# Revit family: VTp731 Тройник 90
name_source: partatom
category: Соединительные детали трубопроводов
revit_build: Autodesk Revit 2015 (Build: 20140606_1530(x64)
units: mm (PartAtom-declared; Revit-internal decimal feet)

## types (9) — shared parameters
Группа модели = VTp.700
Изготовитель = VALTEC S.R.L.
Коэффициент K = 0.5
Метод определения потерь = Коэффициент K
Описание = Тройник 90
Таблица коэффициентов K = Angle Valve Threaded

## per-type parameters (varying)
| type | 110 | 20 | 25 | 32 | 40 | 50 | 63 | 75 | 90 | A | B | d | Код по классификатору | Сц |
| 20 | Нет | Да | Нет | Нет | Нет | Нет | Нет | Нет | Нет | 51 мм | 15 мм | 20 мм | VTp.731.0.020 | 26 мм |
| 25 | Нет | Нет | Да | Нет | Нет | Нет | Нет | Нет | Нет | 59 мм | 17 мм | 25 мм | VTp.731.0.025 | 30 мм |
| 40 | Нет | Нет | Нет | Нет | Да | Нет | Нет | Нет | Нет | 89 мм | 21 мм | 40 мм | VTp.731.0.040 | 44 мм |
| 32 | Нет | Нет | Нет | Да | Нет | Нет | Нет | Нет | Нет | 71 мм | 19 мм | 32 мм | VTp.731.0.032 | 36 мм |
| 50 | Нет | Нет | Нет | Нет | Нет | Да | Нет | Нет | Нет | 106 мм | 24 мм | 50 мм | VTp.731.0.050 | 53 мм |
| 63 | Нет | Нет | Нет | Нет | Нет | Нет | Да | Нет | Нет | 128 мм | 26 мм | 63 мм | VTp.731.0.063 | 64 мм |
| 75 | Нет | Нет | Нет | Нет | Нет | Нет | Нет | Да | Нет | 146 мм | 30 мм | 75 мм | VTp.731.0.075 | 73 мм |
| 90 | Нет | Нет | Нет | Нет | Нет | Нет | Нет | Нет | Да | 172 мм | 33 мм | 90 мм | VTp.731.0.090 | 86 мм |
| 110 | Да | Нет | Нет | Нет | Нет | Нет | Нет | Нет | Нет | 204 мм | 37 мм | 110 мм | VTp.731.0.110 | 102 мм |
